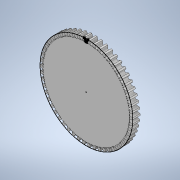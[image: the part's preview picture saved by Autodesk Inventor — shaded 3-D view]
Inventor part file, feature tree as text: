
AUTODESK INVENTOR PART (.ipt)
format: ipt  version: 2022 (Build 260153070, 153G)  size: 387,584 bytes
history: native  units: mm
features: extrude x2, sketch x1, pattern_circular x1
ambient origin geometry x8: Origin, YZ Plane, XZ Plane, XY Plane, X Axis, Y Axis, Z Axis, Center Point
bodies: Solid1 (feature_tree)
feature tree (4):
  sketch  "Sketch1"  dims[d0=3.0mm d1=0.0mm d2=10.0mm d3=0.0mm d4=540.0mm d5=360.0deg]
  extrude  "Extrusion1"  TaperAngle=0.0deg  [1 undecoded]
  extrude  "Extrusion2"  Depth=10.0mm TaperAngle=0.0deg
  pattern_circular  "Circular Pattern1"  Count=54 Angle=360.0deg
note: 1 required parameter value undecoded (feature->parameter linkage not recoverable at this tier; creation-order binding heuristic only, values carry confidence <= 0.55)
